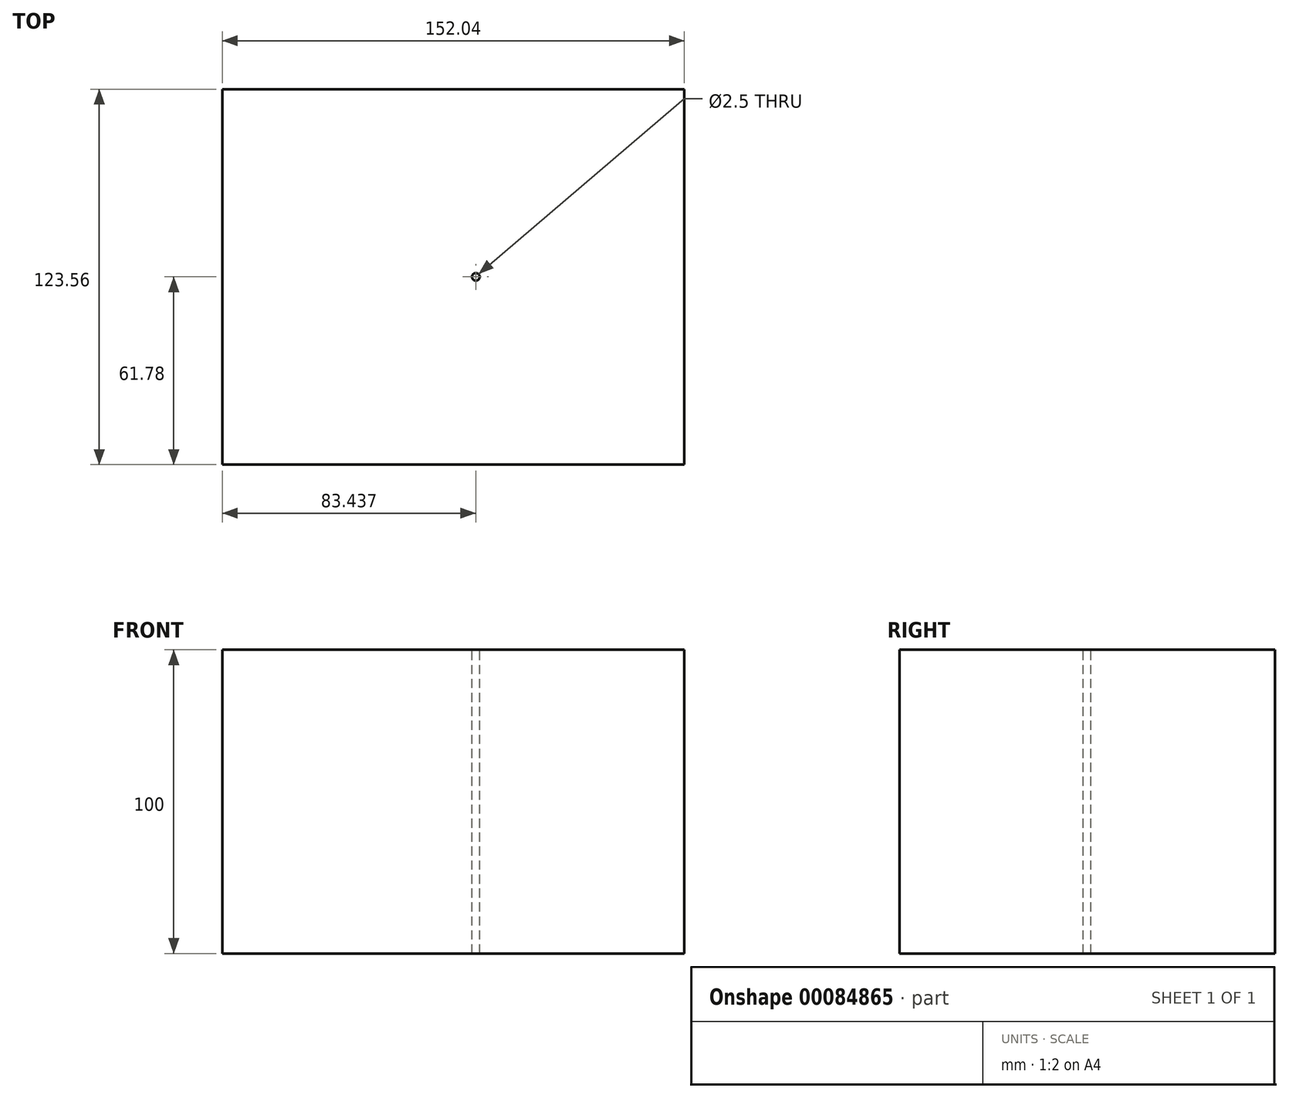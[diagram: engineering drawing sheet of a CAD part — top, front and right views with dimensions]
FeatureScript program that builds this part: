
annotation { "Feature Type Name" : "Feature", "Feature Type Description" : "" }
export const myFeature = defineFeature(function(context is Context, id is Id, definition is map)
    precondition{}
    {
        {
            var Q0;
            Q0=qCreatedBy(makeId("Top.planeOp"),FACE);
            var sketch = newSketch(context, id + "F0", { "sketchPlane" : qUnion([Q0])});
            skLineSegment(sketch, "E0.bottom", {"start": v(76.02, 61.78) * mm, "end": v(-76.02, 61.78) * mm});
            skLineSegment(sketch, "E0.top", {"start": v(76.02, -61.78) * mm, "end": v(-76.02, -61.78) * mm});
            skLineSegment(sketch, "E0.left", {"start": v(76.02, 61.78) * mm, "end": v(76.02, -61.78) * mm});
            skLineSegment(sketch, "E0.right", {"start": v(-76.02, 61.78) * mm, "end": v(-76.02, -61.78) * mm});
            skPoint(sketch, "E0.middle", {"position": v(0, 0) * mm});
            skLineSegment(sketch, "E1.bottom", {"start": v(61.27, -50) * mm, "end": v(-61.27, -50) * mm});
            skLineSegment(sketch, "E1.top", {"start": v(61.27, 50) * mm, "end": v(-61.27, 50) * mm});
            skLineSegment(sketch, "E1.left", {"start": v(63.77, -47.5) * mm, "end": v(63.77, 47.5) * mm});
            skLineSegment(sketch, "E1.right", {"start": v(-63.77, -47.5) * mm, "end": v(-63.77, 47.5) * mm});
            skPoint(sketch, "E2.visualSharp", {"position": v(-63.77, 50) * mm});
            skArc(sketch, "E2.filletArc", {"start": v(-61.27, 50) * mm, "mid": v(-63.04, 49.27) * mm, "end": v(-63.77, 47.5) * mm});
            skPoint(sketch, "E3.visualSharp", {"position": v(63.77, -50) * mm});
            skArc(sketch, "E3.filletArc", {"start": v(61.27, -50) * mm, "mid": v(63.04, -49.27) * mm, "end": v(63.77, -47.5) * mm});
            skPoint(sketch, "E4.visualSharp", {"position": v(63.77, 50) * mm});
            skArc(sketch, "E4.filletArc", {"start": v(63.77, 47.5) * mm, "mid": v(63.04, 49.27) * mm, "end": v(61.27, 50) * mm});
            skPoint(sketch, "E5.visualSharp", {"position": v(-63.77, -50) * mm});
            skArc(sketch, "E5.filletArc", {"start": v(-63.77, -47.5) * mm, "mid": v(-63.04, -49.27) * mm, "end": v(-61.27, -50) * mm});
            skCircle(sketch, "E6", {"center": v(0, 0) * mm, "radius": 10 * mm});
            skSolve(sketch);
        }
        {
            var Q0;
            Q0 = qSketchRegion(id + "F0", true);
            var Q1;
            Q1=makeQuery(id+"F0.imprint","IMPRINT",FACE,{"disambiguationData":[TD([[makeQuery(id+"F0.imprint","IMPRINT",EDGE,{"derivedFrom":sQuery(id+"F0.wireOp",EDGE,"E1.bottom")}),-1.0]])]});
            var Q2;
            Q2=makeQuery(id+"F0.imprint","IMPRINT",FACE,{"disambiguationData":[TD([[makeQuery(id+"F0.imprint","IMPRINT",EDGE,{"derivedFrom":sQuery(id+"F0.wireOp",EDGE,"E6")}),1.0]])]});
            extrude(context, id + "F1", {"entities" : qUnion([Q0, Q1, Q2]), "endBound" : BoundingType.SYMMETRIC, "depth" : 100 * mm});
        }
        {
            var Q0;
            Q0=makeQuery(id+"F1.opExtrude","CAP_FACE",FACE,{"disambiguationData":[OSD([sQuery(id+"F0.wireOp",EDGE,"E0.bottom"),sQuery(id+"F0.wireOp",EDGE,"E0.top"),sQuery(id+"F0.wireOp",EDGE,"E0.left"),sQuery(id+"F0.wireOp",EDGE,"E0.right")])],"isStart":false});
            var sketch = newSketch(context, id + "F2", { "sketchPlane" : qUnion([Q0])});
            skCircle(sketch, "E7", {"center": v(7.42, 0) * mm, "radius": 1.25 * mm});
            skSolve(sketch);
        }
        {
            var Q0;
            Q0 = qSketchRegion(id + "F2", true);
            extrude(context, id + "F3", {"entities" : qUnion([Q0]), "operationType" : NewBodyOperationType.REMOVE, "endBound" : BoundingType.THROUGH_ALL, "oppositeDirection" : true, "depth" : 25.4 * mm});
        }
    });
